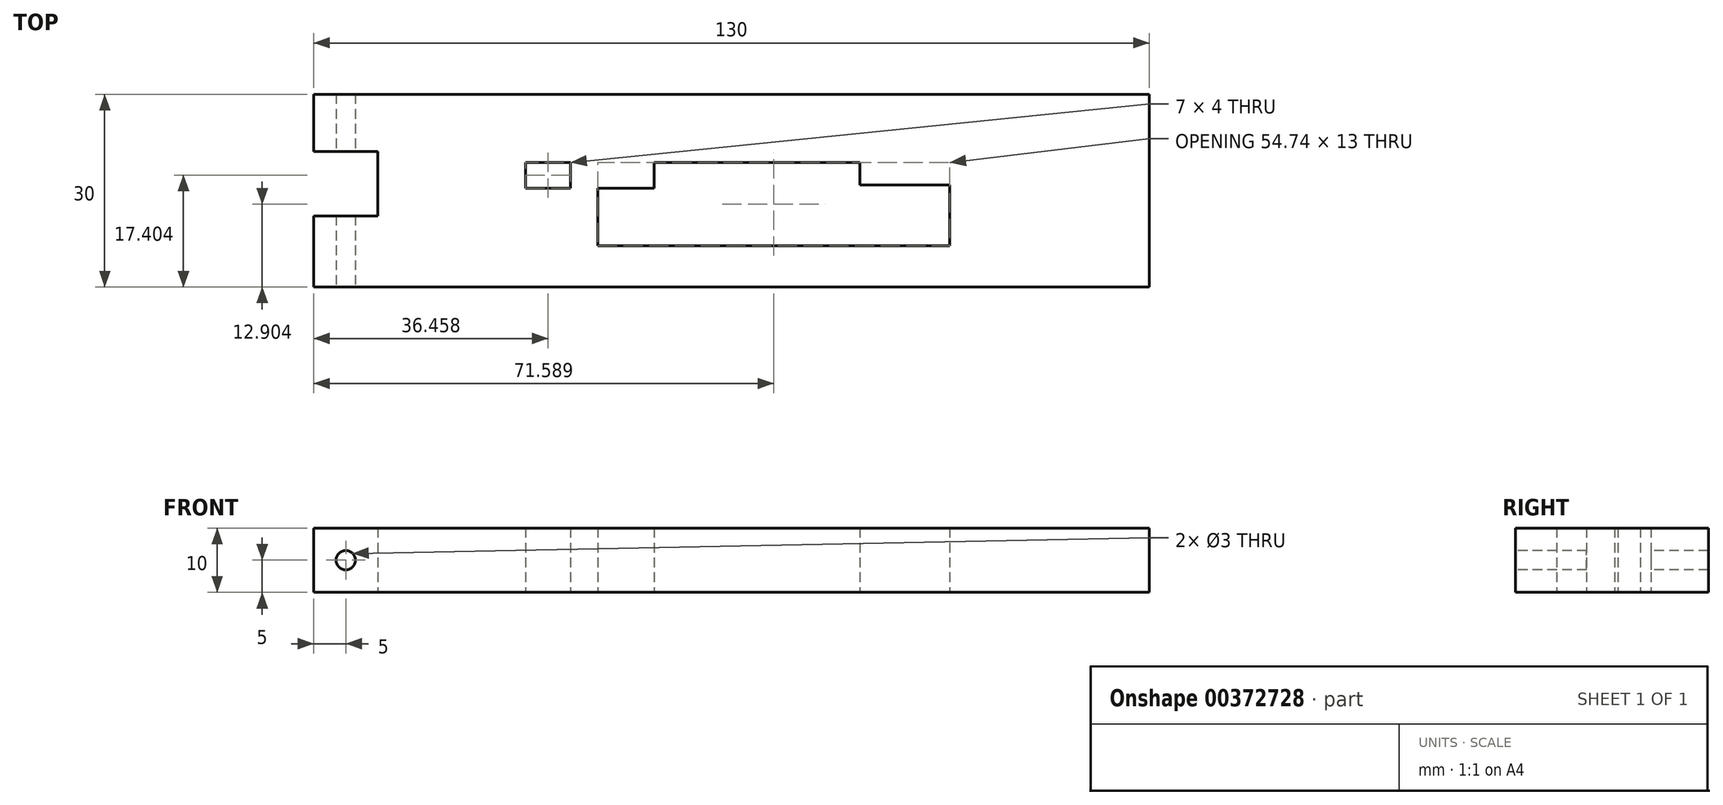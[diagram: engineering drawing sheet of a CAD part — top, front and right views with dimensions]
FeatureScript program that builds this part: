
annotation { "Feature Type Name" : "Feature", "Feature Type Description" : "" }
export const myFeature = defineFeature(function(context is Context, id is Id, definition is map)
    precondition{}
    {
        {
            var Q0;
            Q0=qCreatedBy(makeId("Top.planeOp"),FACE);
            var sketch = newSketch(context, id + "F0", { "sketchPlane" : qUnion([Q0])});
            skPoint(sketch, "E0.middle", {"position": v(0, 0) * mm});
            skLineSegment(sketch, "E1.bottom", {"start": v(-43, 15) * mm, "end": v(43, 15) * mm});
            skLineSegment(sketch, "E1.top", {"start": v(-43, -15) * mm, "end": v(43, -15) * mm});
            skPoint(sketch, "E2.endSnap0", {"position": v(-32.04, 0.4) * mm});
            skLineSegment(sketch, "E3", {"start": v(-12.04, 0.4) * mm, "end": v(-12.04, 4.4) * mm});
            skLineSegment(sketch, "E4", {"start": v(-32.04, 4.4) * mm, "end": v(-25.04, 4.4) * mm});
            skLineSegment(sketch, "E5", {"start": v(-25.04, 4.4) * mm, "end": v(-25.04, 0.4) * mm});
            skLineSegment(sketch, "E6", {"start": v(-25.04, 0.4) * mm, "end": v(-32.04, 0.4) * mm});
            skLineSegment(sketch, "E7", {"start": v(-20.78, -8.6) * mm, "end": v(-20.78, 0.4) * mm});
            skLineSegment(sketch, "E8", {"start": v(-20.78, 0.4) * mm, "end": v(-12.04, 0.4) * mm});
            skLineSegment(sketch, "E9", {"start": v(-12.04, 4.4) * mm, "end": v(19.96, 4.4) * mm});
            skLineSegment(sketch, "E10", {"start": v(19.96, 4.4) * mm, "end": v(19.96, 0.9) * mm});
            skLineSegment(sketch, "E11", {"start": v(19.96, 0.9) * mm, "end": v(33.96, 0.9) * mm});
            skLineSegment(sketch, "E12", {"start": v(33.96, 0.9) * mm, "end": v(33.96, -8.6) * mm});
            skLineSegment(sketch, "E13", {"start": v(33.96, -8.6) * mm, "end": v(-20.78, -8.6) * mm});
            skLineSegment(sketch, "E14", {"start": v(33.96, 0.9) * mm, "end": v(19.96, 0.9) * mm});
            skLineSegment(sketch, "E15", {"start": v(19.96, 0.9) * mm, "end": v(19.96, 4.4) * mm});
            skLineSegment(sketch, "E16", {"start": v(-32.04, 0.4) * mm, "end": v(-32.04, 4.4) * mm});
            skLineSegment(sketch, "E17", {"start": v(-43, 15) * mm, "end": v(-65, 15) * mm});
            skLineSegment(sketch, "E18", {"start": v(-65, 15) * mm, "end": v(-65, -15) * mm});
            skLineSegment(sketch, "E19", {"start": v(-65, -15) * mm, "end": v(-43, -15) * mm});
            skLineSegment(sketch, "E20", {"start": v(43, -15) * mm, "end": v(65, -15) * mm});
            skLineSegment(sketch, "E21", {"start": v(65, -15) * mm, "end": v(65, 15) * mm});
            skLineSegment(sketch, "E22", {"start": v(65, 15) * mm, "end": v(43, 15) * mm});
            skLineSegment(sketch, "E23", {"start": v(-65, 6.07) * mm, "end": v(-55, 6.07) * mm});
            skLineSegment(sketch, "E24", {"start": v(-55, 6.07) * mm, "end": v(-55, -3.93) * mm});
            skLineSegment(sketch, "E25", {"start": v(-55, -3.93) * mm, "end": v(-65, -3.93) * mm});
            skSolve(sketch);
        }
        {
            var Q0;
            Q0=makeQuery(id+"F0.imprint","IMPRINT",FACE,{"disambiguationData":[TD([[makeQuery(id+"F0.imprint","IMPRINT",EDGE,{"derivedFrom":sQuery(id+"F0.wireOp",EDGE,"E1.bottom")}),-1.0]])]});
            extrude(context, id + "F1", {"entities" : qUnion([Q0]), "depth" : 10 * mm});
        }
        {
            var Q0;
            Q0=makeQuery(id+"F1.opExtrude","SWEPT_FACE",FACE,{"disambiguationData":[OSD([sQuery(id+"F0.wireOp",EDGE,"E1.top"),sQuery(id+"F0.wireOp",EDGE,"E19"),sQuery(id+"F0.wireOp",EDGE,"E20")])]});
            var sketch = newSketch(context, id + "F2", { "sketchPlane" : qUnion([Q0])});
            skCircle(sketch, "E26", {"center": v(-60, 5) * mm, "radius": 1.5 * mm});
            skSolve(sketch);
        }
        {
            var Q0;
            Q0=sQuery(id+"F2.wireOp",VERTEX,"E26.center");
            var Q1;
            Q1=makeQuery(id+"F1.opExtrude","SWEPT_BODY",BODY,{"disambiguationData":[OSD([sQuery(id+"F0.wireOp",EDGE,"E1.bottom"),sQuery(id+"F0.wireOp",EDGE,"E1.top"),sQuery(id+"F0.wireOp",EDGE,"E3"),sQuery(id+"F0.wireOp",EDGE,"E4"),sQuery(id+"F0.wireOp",EDGE,"E5"),sQuery(id+"F0.wireOp",EDGE,"E6"),sQuery(id+"F0.wireOp",EDGE,"E7"),sQuery(id+"F0.wireOp",EDGE,"E8"),sQuery(id+"F0.wireOp",EDGE,"E9"),sQuery(id+"F0.wireOp",EDGE,"E12"),sQuery(id+"F0.wireOp",EDGE,"E13"),sQuery(id+"F0.wireOp",EDGE,"E14"),sQuery(id+"F0.wireOp",EDGE,"E15"),sQuery(id+"F0.wireOp",EDGE,"E16"),sQuery(id+"F0.wireOp",EDGE,"E17"),sQuery(id+"F0.wireOp",EDGE,"E18"),sQuery(id+"F0.wireOp",EDGE,"E19"),sQuery(id+"F0.wireOp",EDGE,"E20"),sQuery(id+"F0.wireOp",EDGE,"E21"),sQuery(id+"F0.wireOp",EDGE,"E22"),sQuery(id+"F0.wireOp",EDGE,"E23"),sQuery(id+"F0.wireOp",EDGE,"E24"),sQuery(id+"F0.wireOp",EDGE,"E25")])]});
            hole(context, id + "F3", {"style" : HoleStyle.SIMPLE, "endStyle" : HoleEndStyle.THROUGH, "holeDiameter" : 3 * mm, "isTappedThrough" : true, "tappedDepth" : 12 * mm, "tapClearance" : 3, "startFromSketch" : true, "locations" : qUnion([Q0]), "scope" : qUnion([Q1])});
        }
    });
